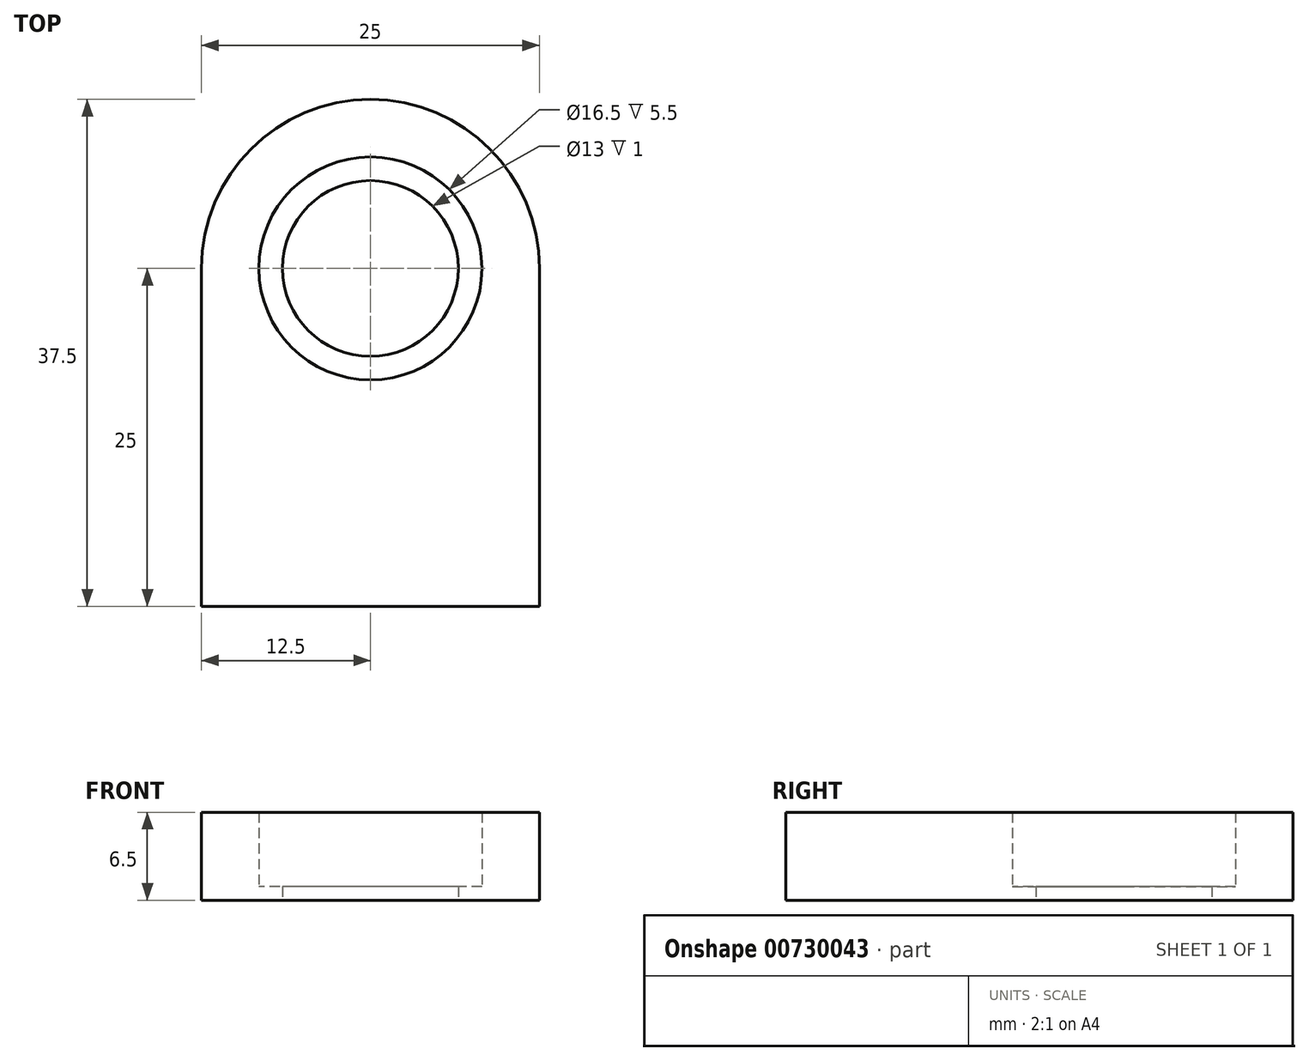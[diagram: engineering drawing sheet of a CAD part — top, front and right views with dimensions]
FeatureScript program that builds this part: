
annotation { "Feature Type Name" : "Feature", "Feature Type Description" : "" }
export const myFeature = defineFeature(function(context is Context, id is Id, definition is map)
    precondition{}
    {
        {
            var Q0;
            Q0=qCreatedBy(makeId("Top.planeOp"),FACE);
            var sketch = newSketch(context, id + "F0", { "sketchPlane" : qUnion([Q0])});
            skArc(sketch, "E0", {"start": v(12.5, 0) * mm, "mid": v(0, 12.5) * mm, "end": v(-12.5, 0) * mm});
            skLineSegment(sketch, "E1", {"start": v(-12.5, 0) * mm, "end": v(-12.5, -25) * mm});
            skLineSegment(sketch, "E2", {"start": v(-12.5, -25) * mm, "end": v(12.5, -25) * mm});
            skLineSegment(sketch, "E3", {"start": v(12.5, -25) * mm, "end": v(12.5, 0) * mm});
            skCircle(sketch, "E4", {"center": v(0, 0) * mm, "radius": 8.25 * mm});
            skCircle(sketch, "E5", {"center": v(0, 0) * mm, "radius": 6.5 * mm});
            skSolve(sketch);
        }
        {
            var Q0;
            Q0=makeQuery(id+"F0.imprint","IMPRINT",FACE,{"disambiguationData":[TD([[makeQuery(id+"F0.imprint","IMPRINT",EDGE,{"derivedFrom":sQuery(id+"F0.wireOp",EDGE,"E0")}),1.0]])]});
            extrude(context, id + "F1", {"entities" : qUnion([Q0]), "depth" : 6.5 * mm, "offsetDistance" : 25 * mm});
        }
        {
            var Q0;
            Q0=makeQuery(id+"F0.imprint","IMPRINT",FACE,{"disambiguationData":[TD([[makeQuery(id+"F0.imprint","IMPRINT",EDGE,{"derivedFrom":sQuery(id+"F0.wireOp",EDGE,"E4")}),1.0]])]});
            extrude(context, id + "F2", {"entities" : qUnion([Q0]), "operationType" : NewBodyOperationType.ADD, "depth" : 1 * mm, "offsetDistance" : 25 * mm});
        }
    });
